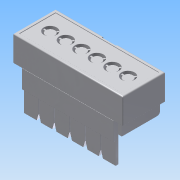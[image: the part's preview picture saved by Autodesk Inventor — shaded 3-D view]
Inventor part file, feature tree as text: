
AUTODESK INVENTOR PART (.ipt)
format: ipt  version: 2015 SP1 (Build 190203100, 203)  size: 581,120 bytes
history: native  units: mm
features: extrude x13, sketch x13, fillet x4, other x2, projected_geometry x1
ambient origin geometry x8: Origin, YZ Plane, XZ Plane, XY Plane, X Axis, Y Axis, Z Axis, Center Point
bodies: Body1 (feature_tree)
feature tree (33):
  other  "Твердое тело1"
  extrude  "Выдавливание1"  Depth=35.8mm
  extrude  "Выдавливание2"  Depth=13.9mm
  extrude  "Выдавливание3"  Depth=1.7mm TaperAngle=0.0deg
  extrude  "Выдавливание4"  Depth=1.0mm
  extrude  "Выдавливание5"  Depth=1.0mm
  extrude  "Выдавливание6"  Depth=1.0mm
  extrude  "Выдавливание7"  Depth=1.0mm
  extrude  "Выдавливание8"  Depth=0.2mm TaperAngle=0.0deg
  extrude  "Выдавливание9"  Depth=4.2mm
  extrude  "Выдавливание10"  Depth=5.2mm
  other  "РабПлоскость1"
  extrude  "Выдавливание11"  Depth=6.95mm
  extrude  "Выдавливание12"  Depth=3.0mm
  extrude  "Выдавливание13"  Depth=0.25mm
  fillet  "Сопряжение1"  Radius=0.25mm
  fillet  "Сопряжение2"  [1 undecoded]
  fillet  "Сопряжение3"  [1 undecoded]
  fillet  "Сопряжение4"  Radius=0.25mm
  sketch  "Эскиз1"
  sketch  "Эскиз2"
  projected_geometry  "Спроецированная петля1"
  sketch  "Эскиз3"
  sketch  "Эскиз4"
  sketch  "Эскиз5"
  sketch  "Эскиз6"
  sketch  "Эскиз7"
  sketch  "Эскиз9"
  sketch  "Эскиз10"
  sketch  "Эскиз11"
  sketch  "Эскиз12"
  sketch  "Эскиз13"
  sketch  "Эскиз14"
note: 2 required parameter values undecoded (feature->parameter linkage not recoverable at this tier; creation-order binding heuristic only, values carry confidence <= 0.55)
